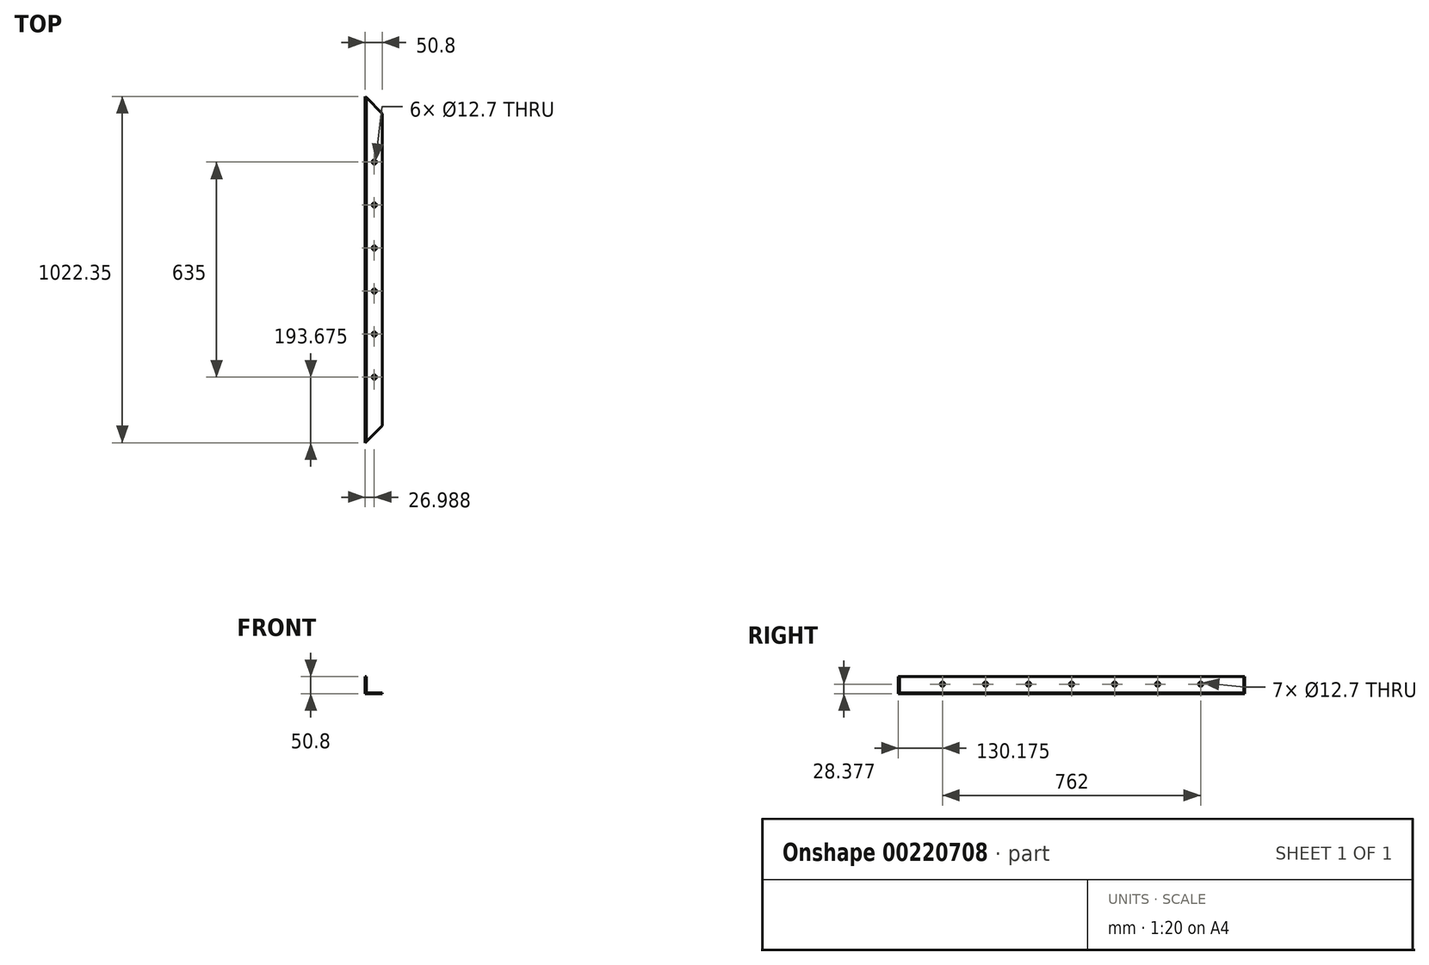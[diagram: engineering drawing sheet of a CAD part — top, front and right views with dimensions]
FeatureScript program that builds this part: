
annotation { "Feature Type Name" : "Feature", "Feature Type Description" : "" }
export const myFeature = defineFeature(function(context is Context, id is Id, definition is map)
    precondition{}
    {
        {
            var Q0;
            Q0=qCreatedBy(makeId("Front.planeOp"),FACE);
            var sketch = newSketch(context, id + "F0", { "sketchPlane" : qUnion([Q0])});
            skLineSegment(sketch, "E0", {"start": v(0, 50.8) * mm, "end": v(3.18, 50.8) * mm});
            skLineSegment(sketch, "E1", {"start": v(3.18, 50.8) * mm, "end": v(3.18, 3.17) * mm});
            skLineSegment(sketch, "E2", {"start": v(3.18, 3.17) * mm, "end": v(50.8, 3.18) * mm});
            skLineSegment(sketch, "E3", {"start": v(50.8, 3.18) * mm, "end": v(50.8, 0) * mm});
            skLineSegment(sketch, "E4", {"start": v(50.8, 0) * mm, "end": v(0, 0) * mm});
            skLineSegment(sketch, "E5", {"start": v(0, 50.8) * mm, "end": v(0, 0) * mm});
            skSolve(sketch);
        }
        {
            var Q0;
            Q0=makeQuery(id+"F0.imprint","IMPRINT",FACE,{"disambiguationData":[TD([[makeQuery(id+"F0.imprint","IMPRINT",EDGE,{"derivedFrom":sQuery(id+"F0.wireOp",EDGE,"E0")}),-1.0]])]});
            extrude(context, id + "F1", {"entities" : qUnion([Q0]), "depth" : 1270 * mm});
        }
        {
            var Q0;
            Q0=makeQuery(id+"F1.opExtrude","SWEPT_FACE",FACE,{"disambiguationData":[OSD([sQuery(id+"F0.wireOp",EDGE,"E4")])]});
            var sketch = newSketch(context, id + "F2", { "sketchPlane" : qUnion([Q0])});
            skLineSegment(sketch, "E6", {"start": v(0, 0) * mm, "end": v(50.8, 50.8) * mm});
            skLineSegment(sketch, "E7", {"start": v(50.8, 50.8) * mm, "end": v(50.8, 971.55) * mm});
            skLineSegment(sketch, "E8", {"start": v(50.8, 971.55) * mm, "end": v(0, 1022.35) * mm});
            skLineSegment(sketch, "E9", {"start": v(0, 1022.35) * mm, "end": v(0, 0) * mm});
            skPoint(sketch, "E10", {"position": v(3.18, 1019.17) * mm});
            skPoint(sketch, "E11", {"position": v(3.18, 3.18) * mm});
            skSolve(sketch);
        }
        {
            var Q0;
            Q0=makeQuery(id+"F2.imprint","IMPRINT",FACE,{"disambiguationData":[TD([[makeQuery(id+"F2.imprint","IMPRINT",EDGE,{"derivedFrom":sQuery(id+"F2.wireOp",EDGE,"E6")}),1.0]])]});
            extrude(context, id + "F3", {"entities" : qUnion([Q0]), "operationType" : NewBodyOperationType.INTERSECT, "oppositeDirection" : true, "depth" : 127 * mm});
        }
        {
            var Q0;
            Q0=makeQuery(id+"F1.opExtrude","SWEPT_FACE",FACE,{"disambiguationData":[OSD([sQuery(id+"F0.wireOp",EDGE,"E1")])]});
            var sketch = newSketch(context, id + "F4", { "sketchPlane" : qUnion([Q0])});
            skLineSegment(sketch, "E12", {"start": v(-1019.17, 28.57) * mm, "end": v(-3.18, 26.99) * mm});
            skCircle(sketch, "E13", {"center": v(-892.18, 28.38) * mm, "radius": 6.35 * mm});
            skCircle(sketch, "E14.1.0.0", {"center": v(-765.18, 28.38) * mm, "radius": 6.35 * mm});
            skCircle(sketch, "E14.2.0.0", {"center": v(-638.18, 28.38) * mm, "radius": 6.35 * mm});
            skCircle(sketch, "E14.3.0.0", {"center": v(-511.18, 28.38) * mm, "radius": 6.35 * mm});
            skCircle(sketch, "E14.4.0.0", {"center": v(-384.18, 28.38) * mm, "radius": 6.35 * mm});
            skCircle(sketch, "E14.5.0.0", {"center": v(-257.18, 28.38) * mm, "radius": 6.35 * mm});
            skCircle(sketch, "E14.6.0.0", {"center": v(-130.18, 28.38) * mm, "radius": 6.35 * mm});
            skLineSegment(sketch, "E14.direction1", {"start": v(-892.18, 28.38) * mm, "end": v(-765.18, 28.38) * mm, "construction": true});
            skPoint(sketch, "E15", {"position": v(-828.68, 28.38) * mm});
            skSolve(sketch);
        }
        {
            var Q0;
            Q0 = qSketchRegion(id + "F4", true);
            extrude(context, id + "F5", {"entities" : qUnion([Q0]), "operationType" : NewBodyOperationType.REMOVE, "oppositeDirection" : true, "depth" : 25.4 * mm});
        }
        {
            var Q0;
            Q0=makeQuery(id+"F1.opExtrude","SWEPT_FACE",FACE,{"disambiguationData":[OSD([sQuery(id+"F0.wireOp",EDGE,"E2")])]});
            var sketch = newSketch(context, id + "F6", { "sketchPlane" : qUnion([Q0])});
            skLineSegment(sketch, "E16", {"start": v(3.18, -1058.96) * mm, "end": v(3.18, -1019.18) * mm});
            skLineSegment(sketch, "E17", {"start": v(3.18, -1058.96) * mm, "end": v(26.99, -1058.96) * mm});
            skPoint(sketch, "E17.endSnap0", {"position": v(26.99, -995.36) * mm});
            skLineSegment(sketch, "E18", {"start": v(26.99, -1058.96) * mm, "end": v(26.99, -828.68) * mm});
            skCircle(sketch, "E19", {"center": v(26.99, -828.68) * mm, "radius": 6.35 * mm});
            skCircle(sketch, "E20.0.1.0", {"center": v(26.99, -701.68) * mm, "radius": 6.35 * mm});
            skCircle(sketch, "E20.0.2.0", {"center": v(26.99, -574.68) * mm, "radius": 6.35 * mm});
            skCircle(sketch, "E20.0.3.0", {"center": v(26.99, -447.68) * mm, "radius": 6.35 * mm});
            skCircle(sketch, "E20.0.4.0", {"center": v(26.99, -320.68) * mm, "radius": 6.35 * mm});
            skCircle(sketch, "E20.0.5.0", {"center": v(26.99, -193.68) * mm, "radius": 6.35 * mm});
            skLineSegment(sketch, "E20.direction1", {"start": v(26.99, -828.68) * mm, "end": v(52.39, -828.68) * mm, "construction": true});
            skLineSegment(sketch, "E20.direction2", {"start": v(26.99, -828.68) * mm, "end": v(26.99, -701.68) * mm, "construction": true});
            skSolve(sketch);
        }
        {
            var Q0;
            Q0=makeQuery(id+"F6.imprint","IMPRINT",FACE,{"disambiguationData":[TD([[makeQuery(id+"F6.imprint","IMPRINT",EDGE,{"derivedFrom":sQuery(id+"F6.wireOp",EDGE,"E19")}),1.0]])]});
            var Q1;
            Q1=makeQuery(id+"F6.imprint","IMPRINT",FACE,{"disambiguationData":[TD([[makeQuery(id+"F6.imprint","IMPRINT",EDGE,{"derivedFrom":sQuery(id+"F6.wireOp",EDGE,"E20.0.1.0")}),1.0]])]});
            var Q2;
            Q2=makeQuery(id+"F6.imprint","IMPRINT",FACE,{"disambiguationData":[TD([[makeQuery(id+"F6.imprint","IMPRINT",EDGE,{"derivedFrom":sQuery(id+"F6.wireOp",EDGE,"E20.0.2.0")}),1.0]])]});
            var Q3;
            Q3=makeQuery(id+"F6.imprint","IMPRINT",FACE,{"disambiguationData":[TD([[makeQuery(id+"F6.imprint","IMPRINT",EDGE,{"derivedFrom":sQuery(id+"F6.wireOp",EDGE,"E20.0.3.0")}),1.0]])]});
            var Q4;
            Q4=makeQuery(id+"F6.imprint","IMPRINT",FACE,{"disambiguationData":[TD([[makeQuery(id+"F6.imprint","IMPRINT",EDGE,{"derivedFrom":sQuery(id+"F6.wireOp",EDGE,"E20.0.5.0")}),1.0]])]});
            var Q5;
            Q5=makeQuery(id+"F6.imprint","IMPRINT",FACE,{"disambiguationData":[TD([[makeQuery(id+"F6.imprint","IMPRINT",EDGE,{"derivedFrom":sQuery(id+"F6.wireOp",EDGE,"E20.0.6.0")}),1.0]])]});
            var Q6;
            Q6=makeQuery(id+"F6.imprint","IMPRINT",FACE,{"disambiguationData":[TD([[makeQuery(id+"F6.imprint","IMPRINT",EDGE,{"derivedFrom":sQuery(id+"F6.wireOp",EDGE,"E20.0.4.0")}),1.0]])]});
            extrude(context, id + "F7", {"entities" : qUnion([Q0, Q1, Q2, Q3, Q4, Q5, Q6]), "operationType" : NewBodyOperationType.REMOVE, "oppositeDirection" : true, "depth" : 25.4 * mm});
        }
    });
